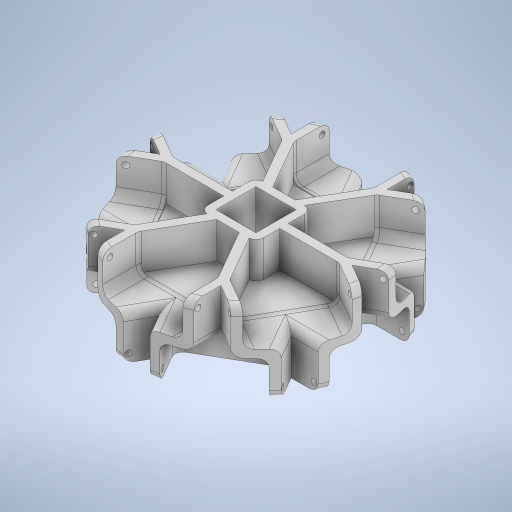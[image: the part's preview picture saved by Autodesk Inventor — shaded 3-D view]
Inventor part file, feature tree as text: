
AUTODESK INVENTOR PART (.ipt)
format: ipt  version: 2024.2 (Build 282272000, 272)  size: 858,112 bytes
history: native  units: mm
features: sketch x10, extrude x9, fillet x7, pattern_circular x7
ambient origin geometry x8: Origin, YZ Plane, XZ Plane, XY Plane, X Axis, Y Axis, Z Axis, Center Point
bodies: Solid1 (feature_tree)
feature tree (33):
  extrude  "Extrusion1"  Depth=12.0mm
  extrude  "Extrusion2"  Depth=20.0mm TaperAngle=360.0deg
  extrude  "Extrusion3"  Depth=12.0mm
  fillet  "Fillet1"  Radius=20.0mm
  pattern_circular  "Circular Pattern1"  Count=6 Angle=360.0deg
  fillet  "Fillet2"  Radius=10.0mm
  pattern_circular  "Circular Pattern2"  Count=6 Angle=360.0deg
  fillet  "Fillet3"  Radius=2.0mm
  fillet  "Fillet4"  Radius=60.0mm
  pattern_circular  "Circular Pattern3"  Angle=60.0deg  [1 undecoded]
  sketch  "Sketch4"  dims[d11=30.0deg d12=60.0mm d14=360.0deg d16=10.0mm d17=0.0mm]
  extrude  "Extrusion4"  Depth=12.0mm
  extrude  "Extrusion5"  Depth=2.0mm
  pattern_circular  "Circular Pattern4"  [2 undecoded]
  fillet  "Fillet5"  [1 undecoded]
  pattern_circular  "Circular Pattern5"  Count=6 Angle=360.0deg
  extrude  "Extrusion6"  Depth=2.0mm
  extrude  "Extrusion7"  Depth=2.0mm TaperAngle=360.0deg
  pattern_circular  "Circular Pattern6"  [2 undecoded]
  fillet  "Fillet6"  Radius=2.0mm
  pattern_circular  "Circular Pattern7"  Angle=60.0deg  [1 undecoded]
  extrude  "Extrusion8"  Depth=12.0mm
  extrude  "Extrusion9"  TaperAngle=0.0deg  [1 undecoded]
  fillet  "Fillet7"  Radius=2.0mm
  sketch  "Sketch1"  dims[d0=60.0mm d1=12.0mm]
  sketch  "Sketch2"  dims[d2=20.0mm d3=60.0mm d5=360.0deg]
  sketch  "Sketch3"  dims[d7=10.0mm d8=0.0mm d9=12.0mm d10=20.0mm]
  sketch  "Sketch5"  dims[d18=2.0mm d19=0.0mm]
  sketch  "Sketch6"  dims[d20=2.0mm d21=60.0mm d22=360.0deg d24=2.0mm]
  sketch  "Sketch7"  dims[d25=60.0mm d26=360.0deg d28=2.0mm d29=2.0mm d30=60.0mm d31=360.0deg]
  sketch  "Sketch8"  dims[d33=2.0mm]
  sketch  "Sketch9"  dims[d35=1.5mm]
  sketch  "Sketch10"  dims[d36=0.0mm d37=0.0mm d38=60.0deg d39=12.0mm d40=2.0mm d41=2.0mm d42=0.0mm d43=0.0mm d44=60.0mm d45=360.0deg d47=2.0mm d48=60.0mm d49=360.0deg d51=2.0mm d52=2.0mm d53=60.0deg d54=12.0mm d55=0.0mm d56=0.0mm d57=2.0mm d58=1.5mm d59=8.5mm d60=0.0mm d61=0.0mm d62=60.0mm d63=360.0deg d65=2.0mm d66=60.0mm d67=360.0deg d69=10.0mm d70=10.0mm d71=0.0mm d72=0.0mm d73=8.5mm d74=14.0mm d75=14.0mm d76=1.0mm d77=10.0mm d78=0.0mm d79=2.0mm d23=0.0mm]
note: 8 required parameter values undecoded (feature->parameter linkage not recoverable at this tier; creation-order binding heuristic only, values carry confidence <= 0.55)
